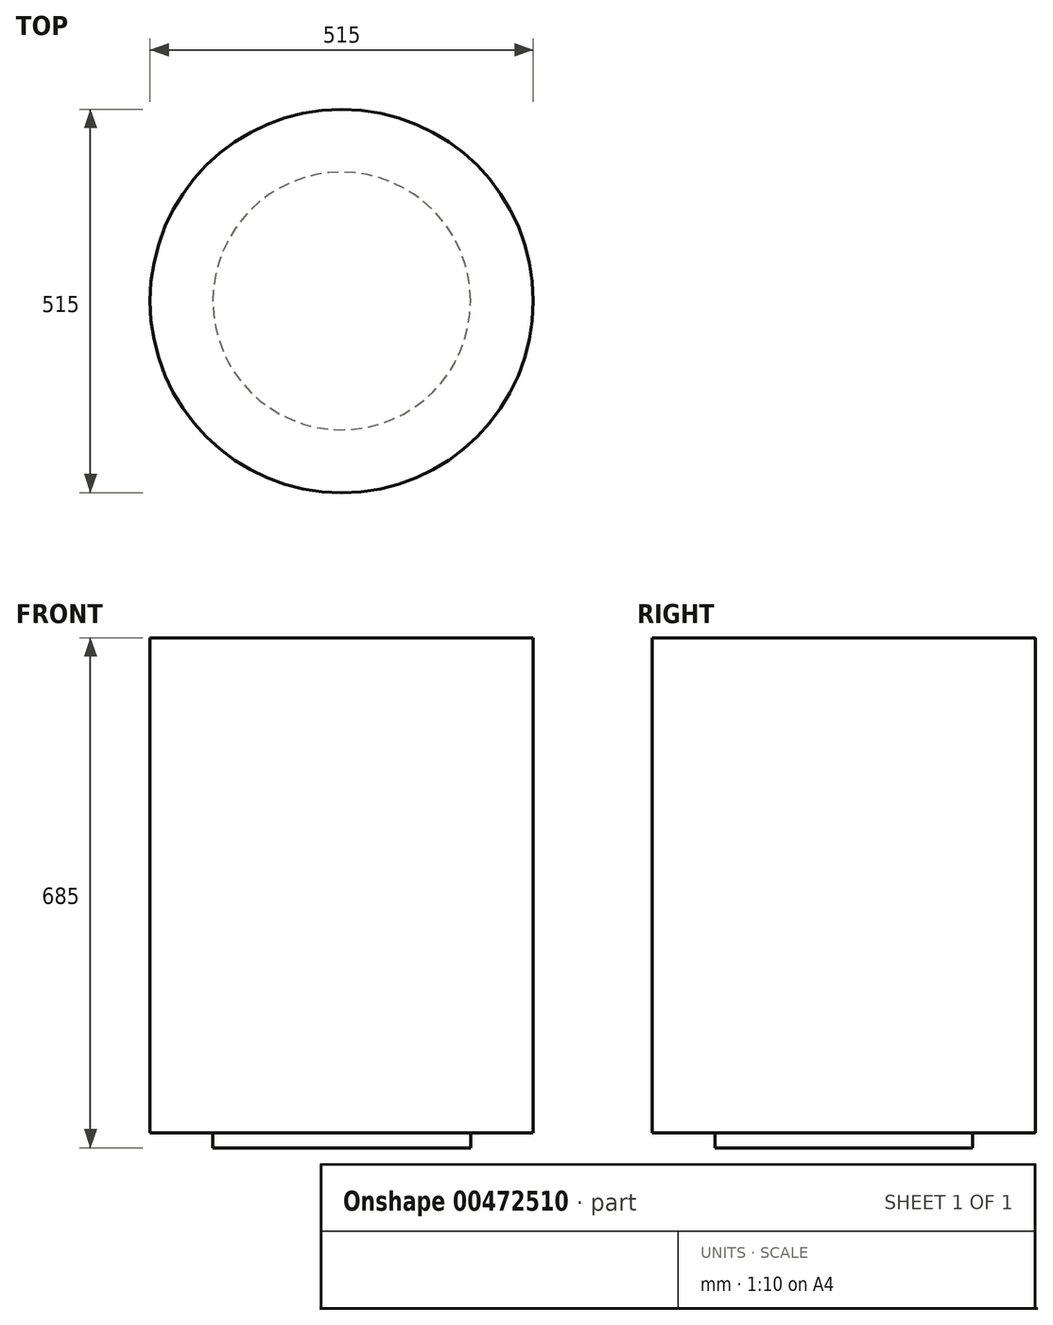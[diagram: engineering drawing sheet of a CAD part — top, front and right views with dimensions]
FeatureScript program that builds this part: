
annotation { "Feature Type Name" : "Feature", "Feature Type Description" : "" }
export const myFeature = defineFeature(function(context is Context, id is Id, definition is map)
    precondition{}
    {
        {
            var Q0;
            Q0=qCreatedBy(makeId("Top.planeOp"),FACE);
            var sketch = newSketch(context, id + "F0", { "sketchPlane" : qUnion([Q0])});
            skCircle(sketch, "E0", {"center": v(0, 0) * mm, "radius": 257.5 * mm});
            skSolve(sketch);
        }
        {
            var Q0;
            Q0 = qSketchRegion(id + "F0", true);
            extrude(context, id + "F1", {"entities" : qUnion([Q0]), "depth" : 665 * mm, "offsetDistance" : 25 * mm});
        }
        {
            var Q0;
            Q0=makeQuery(id+"F1.opExtrude","CAP_FACE",FACE,{"disambiguationData":[OSD([sQuery(id+"F0.wireOp",EDGE,"E0")])],"isStart":true});
            var sketch = newSketch(context, id + "F2", { "sketchPlane" : qUnion([Q0])});
            skCircle(sketch, "E1", {"center": v(0, 0) * mm, "radius": 173.1 * mm});
            skSolve(sketch);
        }
        {
            var Q0;
            Q0 = qSketchRegion(id + "F2", true);
            extrude(context, id + "F3", {"entities" : qUnion([Q0]), "operationType" : NewBodyOperationType.ADD, "depth" : 20 * mm, "offsetDistance" : 25 * mm});
        }
    });
